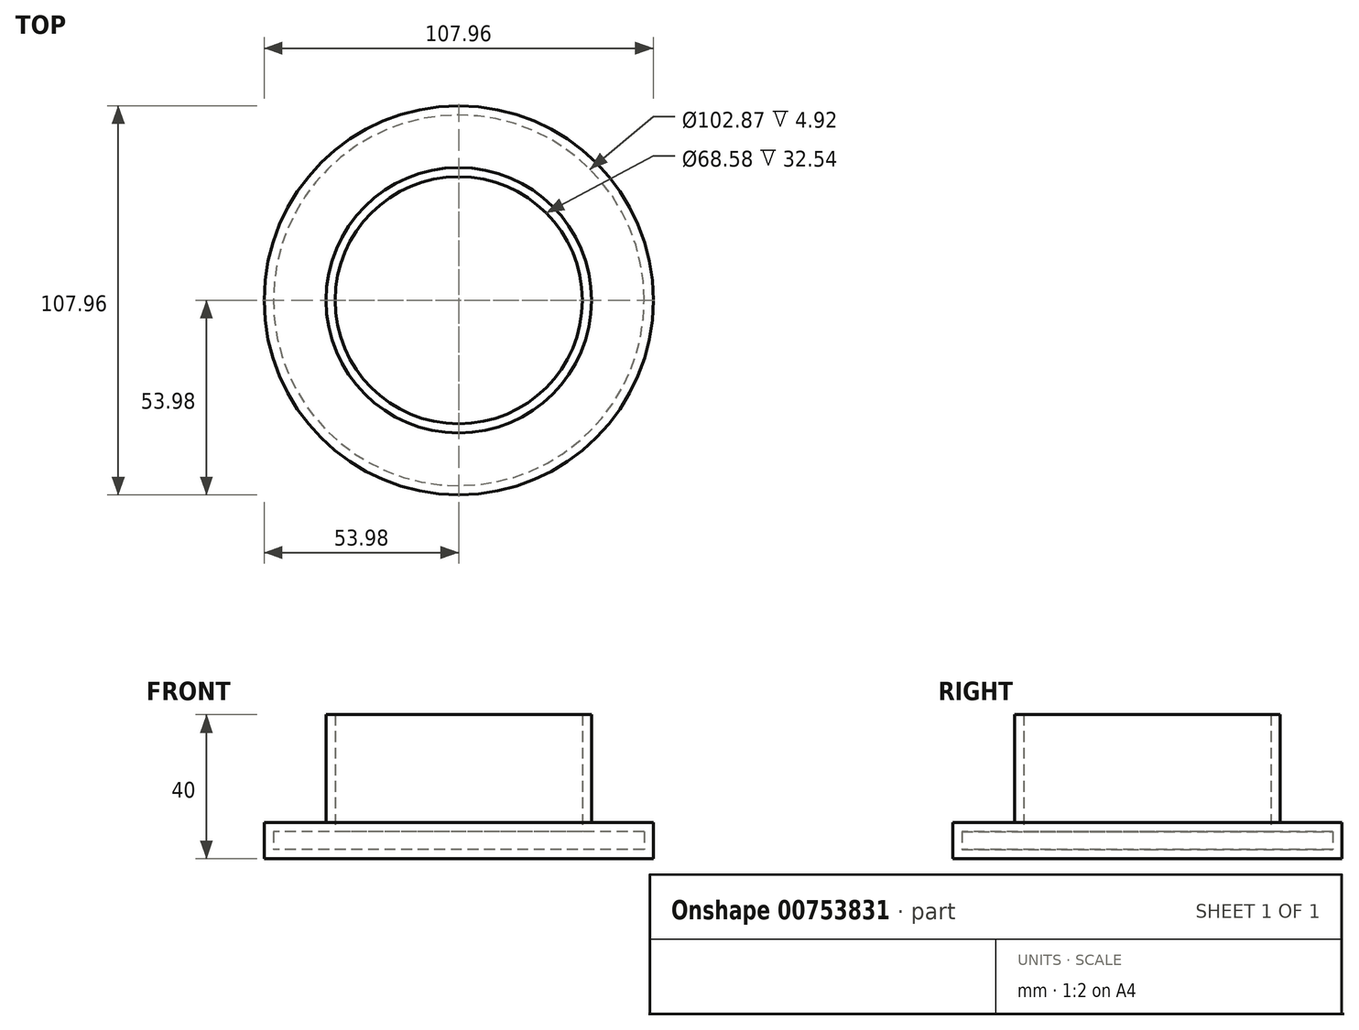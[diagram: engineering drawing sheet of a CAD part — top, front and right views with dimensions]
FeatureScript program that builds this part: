
annotation { "Feature Type Name" : "Feature", "Feature Type Description" : "" }
export const myFeature = defineFeature(function(context is Context, id is Id, definition is map)
    precondition{}
    {
        {
            var Q0;
            Q0=qCreatedBy(makeId("Top.planeOp"),FACE);
            var sketch = newSketch(context, id + "F0", { "sketchPlane" : qUnion([Q0])});
            skCircle(sketch, "E0", {"center": v(0, 0) * mm, "radius": 36.83 * mm});
            skSolve(sketch);
        }
        {
            var Q0;
            Q0=qCreatedBy(makeId("Top.planeOp"),FACE);
            var sketch = newSketch(context, id + "F1", { "sketchPlane" : qUnion([Q0])});
            skCircle(sketch, "E1", {"center": v(0, 0) * mm, "radius": 53.98 * mm});
            skSolve(sketch);
        }
        {
            var Q0;
            Q0=makeQuery(id+"F0.imprint","IMPRINT",FACE,{"disambiguationData":[TD([[makeQuery(id+"F0.imprint","IMPRINT",EDGE,{"derivedFrom":sQuery(id+"F0.wireOp",EDGE,"E0")}),1.0]])]});
            var sketch = newSketch(context, id + "F2", { "sketchPlane" : qUnion([Q0])});
            skCircle(sketch, "E2", {"center": v(0, 0) * mm, "radius": 34.3 * mm});
            skSolve(sketch);
        }
        {
            var Q0;
            Q0=makeQuery(id+"F1.imprint","IMPRINT",FACE,{"disambiguationData":[TD([[makeQuery(id+"F1.imprint","IMPRINT",EDGE,{"derivedFrom":sQuery(id+"F1.wireOp",EDGE,"E1")}),1.0]])]});
            extrude(context, id + "F3", {"entities" : qUnion([Q0]), "depth" : 10 * mm, "offsetDistance" : 25.4 * mm});
        }
        {
            var Q0;
            Q0 = qSketchRegion(id + "F0", true);
            extrude(context, id + "F4", {"entities" : qUnion([Q0]), "operationType" : NewBodyOperationType.ADD, "depth" : 40 * mm, "offsetDistance" : 25.4 * mm});
        }
        {
            var Q0;
            Q0=makeQuery(id+"F4.opExtrude","CAP_FACE",FACE,{"disambiguationData":[OSD([sQuery(id+"F0.wireOp",EDGE,"E0")])],"isStart":false});
            shell(context, id + "F5", {"entities" : qUnion([Q0]), "thickness" : 2.54 * mm});
        }
    });
